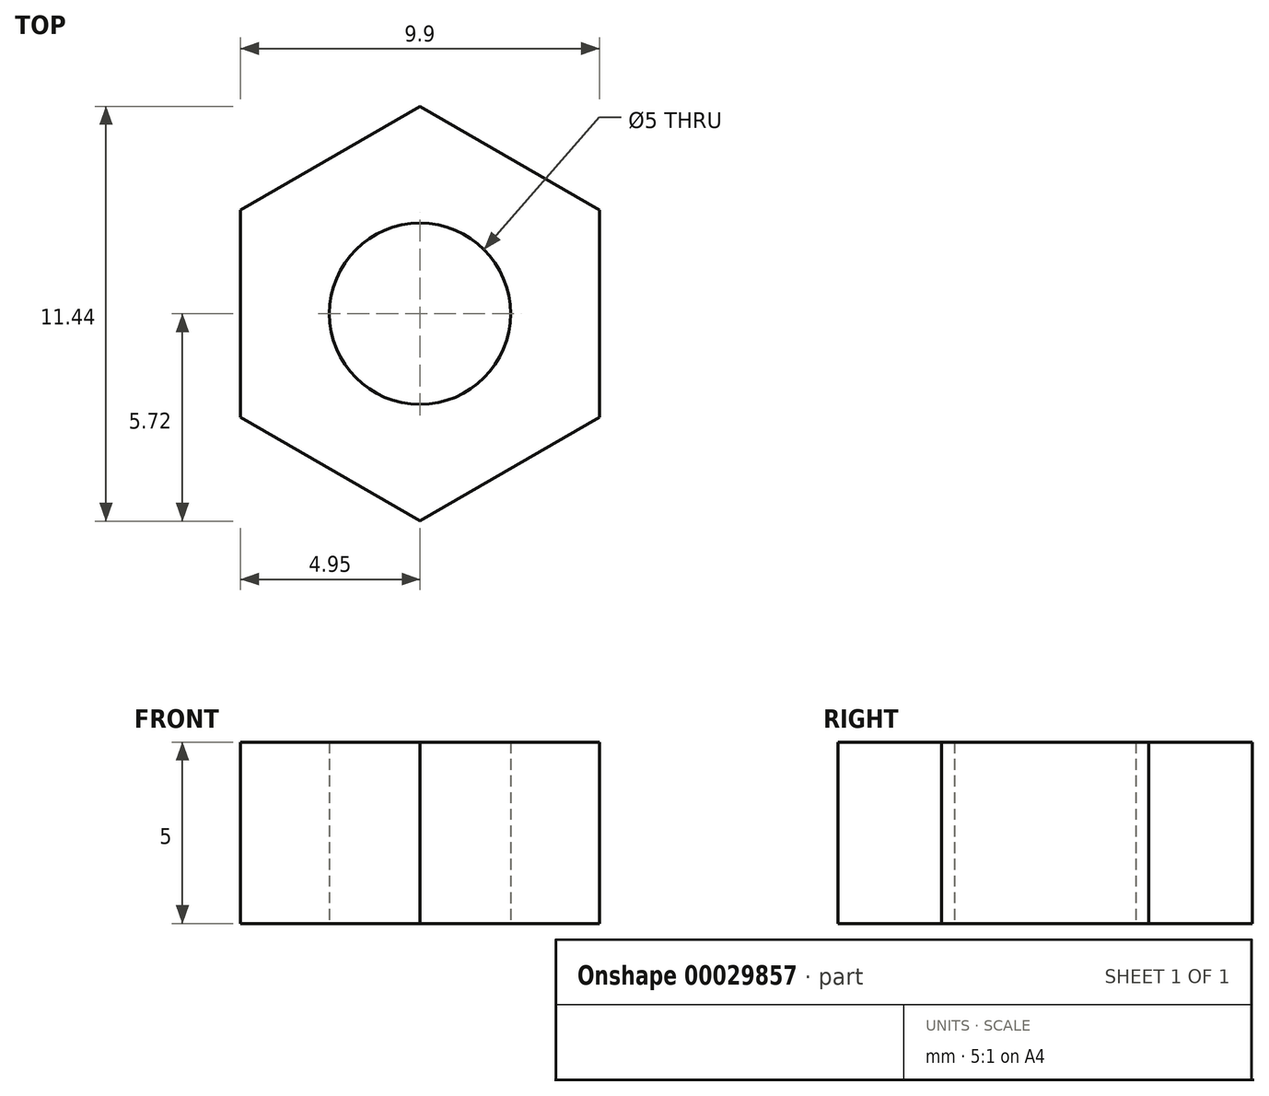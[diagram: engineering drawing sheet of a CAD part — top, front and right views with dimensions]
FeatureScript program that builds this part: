
annotation { "Feature Type Name" : "Feature", "Feature Type Description" : "" }
export const myFeature = defineFeature(function(context is Context, id is Id, definition is map)
    precondition{}
    {
        {
            var Q0;
            Q0=qCreatedBy(makeId("Top.planeOp"),FACE);
            var sketch = newSketch(context, id + "F0", { "sketchPlane" : qUnion([Q0])});
            skCircle(sketch, "E0.cCircle", {"center": v(0, 0) * mm, "radius": 4.95 * mm, "construction": true});
            skLineSegment(sketch, "E0.0", {"start": v(-4.95, -2.86) * mm, "end": v(-4.95, 2.86) * mm});
            skLineSegment(sketch, "E0.1", {"start": v(-4.95, 2.86) * mm, "end": v(0, 5.72) * mm});
            skLineSegment(sketch, "E0.2", {"start": v(0, 5.72) * mm, "end": v(4.95, 2.86) * mm});
            skLineSegment(sketch, "E0.3", {"start": v(4.95, 2.86) * mm, "end": v(4.95, -2.86) * mm});
            skLineSegment(sketch, "E0.4", {"start": v(4.95, -2.86) * mm, "end": v(0, -5.72) * mm});
            skLineSegment(sketch, "E0.5", {"start": v(0, -5.72) * mm, "end": v(-4.95, -2.86) * mm});
            skPoint(sketch, "E0.0.midPoint", {"position": v(-4.95, 0) * mm});
            skCircle(sketch, "E1", {"center": v(0, 0) * mm, "radius": 2.5 * mm});
            skSolve(sketch);
        }
        {
            var Q0;
            Q0=makeQuery(id+"F0.imprint","IMPRINT",FACE,{"disambiguationData":[TD([[makeQuery(id+"F0.imprint","IMPRINT",EDGE,{"derivedFrom":sQuery(id+"F0.wireOp",EDGE,"E0.0")}),-1.0]])]});
            extrude(context, id + "F1", {"entities" : qUnion([Q0]), "depth" : 5 * mm});
        }
    });
